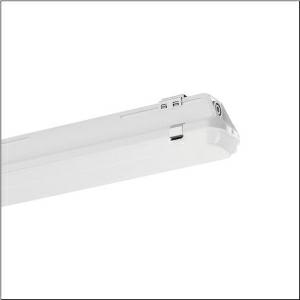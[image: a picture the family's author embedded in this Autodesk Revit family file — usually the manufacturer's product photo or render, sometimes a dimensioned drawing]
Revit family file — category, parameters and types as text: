
# Revit family: monsun_11_emergency_51fp107p437l3g
name_source: partatom
category: Lighting Fixtures
units: mm (PartAtom-declared; Revit-internal decimal feet)

## family parameters
Cut with Voids When Loaded = No
Host = Face
Light Source = No
Part Type = Normal
Room Calculation Point = No
Round Connector Dimension = Use Diameter
Shared = No

## types (1)
- --- (1 x LED, 3840 lm, 24.9 W, 4000K)
    Apparent Load = 25 VA
    CIE Flux Codes = 47 77 93 94 100
    Color Rendering = 80
    Color Temperature = 4000K
    Default Elevation = 1800 mm
    Description = Monsun 11 emergency, damp-proof luminaire, chain hanger, primary optical cover: enclosure, of PMMA, light emission: direct distribution, primary light characteristic: symmetric, installation type: suspended mounting, surface-mounted, horizontal mounting, vertical mounting, LED, rated luminous flux: 3.840lm, luminous efficacy: 182lm/W, light colour: 840, colour temperature: 4000K, control gear: ON/OFF, with terminal, 3-pole, max. 2.5mm², mains connection: 220..240V, AC, 50/60Hz, rated input power: 25W, control gear: single battery element, battery: LiFePO4, 9Ah, luminaire housing, of glass-fibre reinforced polyester, uncoated, bright grey, incl. chain hanger, length: 1.590mm, width: 90mm, height: 88mm, clip for enclosure, of stainless steel (V2A), ceiling mounting element, of stainless steel (V2A), chain hanger, of stainless steel (V2A), protection rating (complete): IP66, insulation class (complete): insulation class I (protective earthing), certification: CE, ENEC, VDE, UKCA, protection symbol: D, impact resistance: IK04, permissible operating ambient temperature: +5..+35°C, standard: EN 50419, EN 60598-2-1, contact your sales advisor before using the luminaires in applications with unclear chemical exposure, large temperature fluctuations or condensation-forming humidity, LABS conformity tested according to VDMA 24364:2018-05, no direct snow, no direct sun, no direct rain, for indoor or canopied outdoor use, corresponds to IFS (International Featured Standards) requirements for safety and quality in the food industry, packaging unit: 1 piece
    Height = 89 mm
    Lamp = 1 x LED
    Lamp Light Flux = 3840 lm
    Lamp Power = 24.9 W
    Lamp count = 1
    Length = 1590 mm
    Luminous efficacy = 154 lm/W
    Manufacturer = Siteco
    ModVariant = No
    Model = 51FP107P437L3G
    Mounting Place = Ceiling
    Mounting Type = Surface mounted
    Number of Poles = 1
    OnlyDefault = Yes
    Power Factor = 1
    Product Name = Monsun 11 emergency
    Product group = damp-proof luminaire
    ProductGroupID = 300
    Protection Class = Protection class I
    Protection Degree = IP 66
    RLX_Detail_Level = 1
    RLX_Emergency_Light_Flux = 0 lm
    RLX_Emergency_Type = 0
    RLX_Emergency_Type_DB = No
    RlxData = <blob elided: 88873 chars, md5=cd8c062a>
    Socket = socket
    Standby Power = 0 W
    System Light Flux = 3840 lm
    System Power = 25 W
    Type Comments = : AC-mode
    Type Image = l_1349237.jpg
    URL = http://relux.com
    VarID = @adj_030287
    Voltage = 0 V
    Weight = 0.00 kg
    Width = 90 mm

## geometry (parser evidence)
native form markers: Blend x4, Sweep x11
no freeform markers — native parametric forms only
